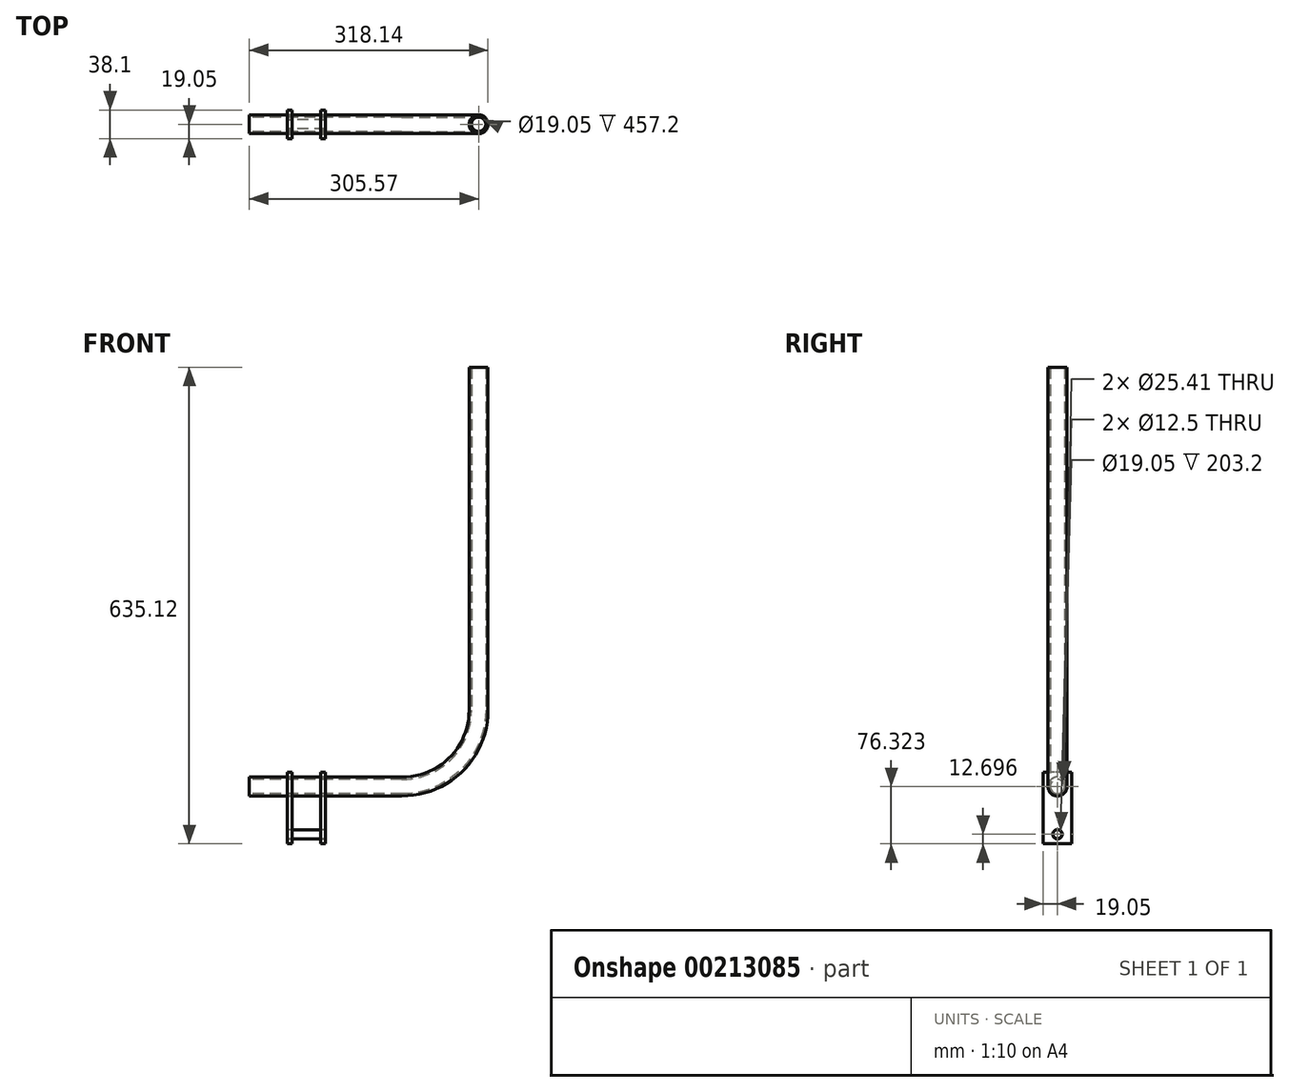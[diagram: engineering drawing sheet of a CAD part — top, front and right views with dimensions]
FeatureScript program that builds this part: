
annotation { "Feature Type Name" : "Feature", "Feature Type Description" : "" }
export const myFeature = defineFeature(function(context is Context, id is Id, definition is map)
    precondition{}
    {
        {
            var Q0;
            Q0=qCreatedBy(makeId("Top.planeOp"),FACE);
            var sketch = newSketch(context, id + "F0", { "sketchPlane" : qUnion([Q0])});
            skCircle(sketch, "E0", {"center": v(0, 0) * mm, "radius": 12.57 * mm});
            skCircle(sketch, "E1.0", {"center": v(0, 0) * mm, "radius": 9.53 * mm});
            skSolve(sketch);
        }
        {
            var Q0;
            Q0=qCreatedBy(makeId("Front.planeOp"),FACE);
            var sketch = newSketch(context, id + "F1", { "sketchPlane" : qUnion([Q0])});
            skLineSegment(sketch, "E2", {"start": v(0, 0) * mm, "end": v(0, -457.2) * mm});
            skArc(sketch, "E3", {"start": v(0, -457.2) * mm, "mid": v(-30.03, -529.32) * mm, "end": v(-102.37, -558.8) * mm});
            skLineSegment(sketch, "E4", {"start": v(0, -457.2) * mm, "end": v(0, -558.8) * mm, "construction": true});
            skLineSegment(sketch, "E5", {"start": v(-305.57, -558.8) * mm, "end": v(-102.37, -558.8) * mm});
            skSolve(sketch);
        }
        {
            var Q0;
            Q0=makeQuery(id+"F0.imprint","IMPRINT",FACE,{"disambiguationData":[TD([[makeQuery(id+"F0.imprint","IMPRINT",EDGE,{"derivedFrom":sQuery(id+"F0.wireOp",EDGE,"E0")}),1.0]])]});
            var Q1;
            Q1=sQuery(id+"F1.wireOp",EDGE,"E2");
            var Q2;
            Q2=sQuery(id+"F1.wireOp",EDGE,"E3");
            var Q3;
            Q3=sQuery(id+"F1.wireOp",EDGE,"E5");
            sweep(context, id + "F2", {"profiles" : qUnion([Q0]), "path" : qUnion([Q1, Q2, Q3])});
        }
        {
            var Q0;
            Q0=makeQuery(id+"F2.opSweep","CAP_FACE",FACE,{"disambiguationData":[OSD([sQuery(id+"F0.wireOp",EDGE,"E0"),sQuery(id+"F0.wireOp",EDGE,"E1.0"),sQuery(id+"F1.wireOp",VERTEX,"E5.start")])],"isStart":false});
            cPlane(context, id + "F3", {"entities" : qUnion([Q0]), "cplaneType" : CPlaneType.OFFSET, "offset" : 101.6 * mm, "oppositeDirection" : true, "width" : 152.4 * mm, "height" : 152.4 * mm});
        }
        {
            var Q0;
            Q0=qCreatedBy(id+"F3.planeOp",FACE);
            var sketch = newSketch(context, id + "F4", { "sketchPlane" : qUnion([Q0])});
            skLineSegment(sketch, "E6", {"start": v(-34.7, -523.99) * mm, "end": v(-33.44, -523.99) * mm, "construction": true});
            skLineSegment(sketch, "E7", {"start": v(0, -546.22) * mm, "end": v(0, -539.87) * mm, "construction": true});
            skLineSegment(sketch, "E8", {"start": v(0, -546.22) * mm, "end": v(0, -635.12) * mm, "construction": true});
            skLineSegment(sketch, "E9", {"start": v(0, -539.87) * mm, "end": v(19.05, -539.87) * mm, "construction": true});
            skLineSegment(sketch, "E10", {"start": v(0, -539.87) * mm, "end": v(-19.05, -539.87) * mm, "construction": true});
            skLineSegment(sketch, "E11", {"start": v(19.05, -635.12) * mm, "end": v(0, -635.12) * mm, "construction": true});
            skLineSegment(sketch, "E12", {"start": v(0, -635.12) * mm, "end": v(-19.05, -635.12) * mm, "construction": true});
            skLineSegment(sketch, "E13", {"start": v(-19.05, -539.87) * mm, "end": v(19.05, -539.87) * mm});
            skLineSegment(sketch, "E14", {"start": v(19.05, -539.87) * mm, "end": v(19.05, -635.12) * mm});
            skLineSegment(sketch, "E15", {"start": v(19.05, -635.12) * mm, "end": v(-19.05, -635.12) * mm});
            skLineSegment(sketch, "E16", {"start": v(-19.05, -635.12) * mm, "end": v(-19.05, -539.87) * mm});
            skPoint(sketch, "E17", {"position": v(0, -558.8) * mm});
            skCircle(sketch, "E18", {"center": v(0, -558.8) * mm, "radius": 12.7 * mm});
            skLineSegment(sketch, "E19", {"start": v(0, -635.12) * mm, "end": v(0, -622.42) * mm, "construction": true});
            skCircle(sketch, "E20", {"center": v(0, -622.42) * mm, "radius": 6.25 * mm});
            skSolve(sketch);
        }
        {
            var Q0;
            Q0=makeQuery(id+"F4.imprint","IMPRINT",FACE,{"disambiguationData":[TD([[makeQuery(id+"F4.imprint","IMPRINT",EDGE,{"derivedFrom":sQuery(id+"F4.wireOp",EDGE,"E13")}),-1.0]])]});
            extrude(context, id + "F5", {"entities" : qUnion([Q0]), "depth" : 6.35 * mm});
        }
        {
            var Q0;
            Q0=makeQuery(id+"F5.opExtrude","SWEPT_BODY",BODY,{"disambiguationData":[OSD([sQuery(id+"F4.wireOp",EDGE,"E13"),sQuery(id+"F4.wireOp",EDGE,"E14"),sQuery(id+"F4.wireOp",EDGE,"E15"),sQuery(id+"F4.wireOp",EDGE,"E16"),sQuery(id+"F4.wireOp",EDGE,"E18"),sQuery(id+"F4.wireOp",EDGE,"E20")])]});
            transform(context, id + "F6", {"entities" : qUnion([Q0]), "transformType" : TransformType.TRANSLATION_3D, "dx" : -44.45 * mm, "dy" : 0 * mm, "dz" : 0 * mm, "makeCopy" : true});
        }
        {
            var Q0;
            Q0=makeQuery(id+"F6.opPattern","COPY",FACE,{"derivedFrom":makeQuery(id+"F5.opExtrude","CAP_FACE",FACE,{"disambiguationData":[OSD([sQuery(id+"F4.wireOp",EDGE,"E13"),sQuery(id+"F4.wireOp",EDGE,"E14"),sQuery(id+"F4.wireOp",EDGE,"E15"),sQuery(id+"F4.wireOp",EDGE,"E16"),sQuery(id+"F4.wireOp",EDGE,"E18"),sQuery(id+"F4.wireOp",EDGE,"E20")])],"isStart":false}),"instanceName":"1"});
            var sketch = newSketch(context, id + "F7", { "sketchPlane" : qUnion([Q0])});
            skCircle(sketch, "E21", {"center": v(0, -622.42) * mm, "radius": 6 * mm});
            skSolve(sketch);
        }
        {
            var Q0;
            Q0=makeQuery(id+"F7.imprint","IMPRINT",FACE,{"disambiguationData":[TD([[makeQuery(id+"F7.imprint","IMPRINT",EDGE,{"derivedFrom":sQuery(id+"F7.wireOp",EDGE,"E21")}),1.0]])]});
            extrude(context, id + "F8", {"entities" : qUnion([Q0]), "oppositeDirection" : true, "depth" : 50.8 * mm});
        }
    });
